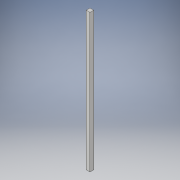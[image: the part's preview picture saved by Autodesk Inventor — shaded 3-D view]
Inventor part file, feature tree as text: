
AUTODESK INVENTOR PART (.ipt)
format: ipt  version: 2017 (Build 210142000, 142)  size: 91,136 bytes
history: native  units: in
note: dims shown in document units (in); Inventor stores cm internally (conversion verified against a paired STEP export)
features: extrude x1, sketch x1
ambient origin geometry x8: Origin, YZ Plane, XZ Plane, XY Plane, X Axis, Y Axis, Z Axis, Center Point
bodies: Solid1 (feature_tree)
feature tree (2):
  extrude  "Extrusion1"  Depth=9.0in
  sketch  "Sketch1"  dims[d0=0.25in d1=9.0in d2=0.25in d3=0.0in]
